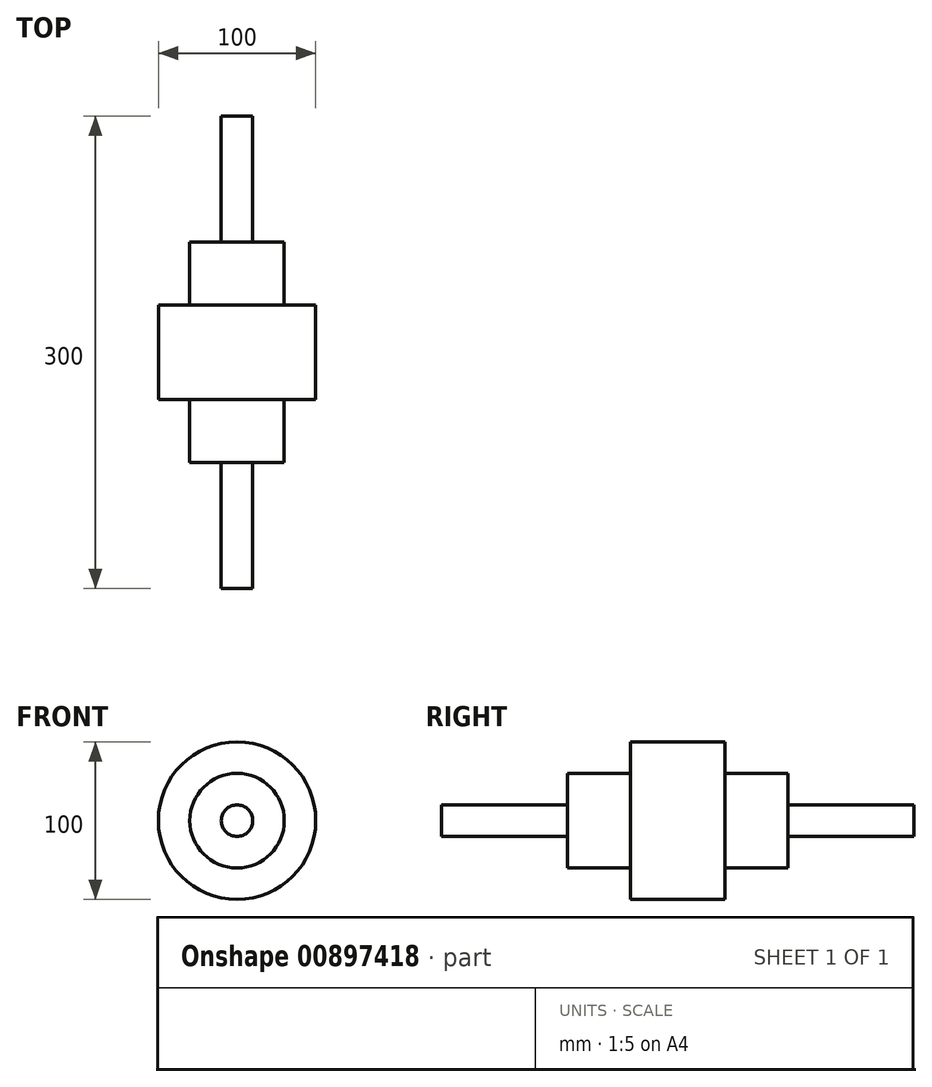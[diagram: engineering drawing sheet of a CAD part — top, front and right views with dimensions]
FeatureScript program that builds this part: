
annotation { "Feature Type Name" : "Feature", "Feature Type Description" : "" }
export const myFeature = defineFeature(function(context is Context, id is Id, definition is map)
    precondition{}
    {
        {
            var Q0;
            Q0=qCreatedBy(makeId("Front.planeOp"),FACE);
            var sketch = newSketch(context, id + "F0", { "sketchPlane" : qUnion([Q0])});
            skCircle(sketch, "E0", {"center": v(0, 0) * mm, "radius": 50 * mm});
            skSolve(sketch);
        }
        {
            var Q0;
            Q0=makeQuery(id+"F0.imprint","IMPRINT",FACE,{"disambiguationData":[TD([[makeQuery(id+"F0.imprint","IMPRINT",EDGE,{"derivedFrom":sQuery(id+"F0.wireOp",EDGE,"E0")}),1.0]])]});
            extrude(context, id + "F1", {"entities" : qUnion([Q0]), "depth" : 60 * mm, "offsetDistance" : 25.4 * mm});
        }
        {
            var Q0;
            Q0=makeQuery(id+"F1.opExtrude","CAP_FACE",FACE,{"disambiguationData":[OSD([sQuery(id+"F0.wireOp",EDGE,"E0")])],"isStart":false});
            var sketch = newSketch(context, id + "F2", { "sketchPlane" : qUnion([Q0])});
            skCircle(sketch, "E1", {"center": v(0, 0) * mm, "radius": 30 * mm});
            skSolve(sketch);
        }
        {
            var Q0;
            Q0=makeQuery(id+"F2.imprint","IMPRINT",FACE,{"disambiguationData":[TD([[makeQuery(id+"F2.imprint","IMPRINT",EDGE,{"derivedFrom":sQuery(id+"F2.wireOp",EDGE,"E1")}),1.0]])]});
            extrude(context, id + "F3", {"entities" : qUnion([Q0]), "operationType" : NewBodyOperationType.ADD, "depth" : 40 * mm, "offsetDistance" : 25.4 * mm});
        }
        {
            var Q0;
            Q0=makeQuery(id+"F3.opExtrude","CAP_FACE",FACE,{"disambiguationData":[OSD([sQuery(id+"F2.wireOp",EDGE,"E1")])],"isStart":false});
            var sketch = newSketch(context, id + "F4", { "sketchPlane" : qUnion([Q0])});
            skCircle(sketch, "E2", {"center": v(0, 0) * mm, "radius": 10 * mm});
            skSolve(sketch);
        }
        {
            var Q0;
            Q0=makeQuery(id+"F4.imprint","IMPRINT",FACE,{"disambiguationData":[TD([[makeQuery(id+"F4.imprint","IMPRINT",EDGE,{"derivedFrom":sQuery(id+"F4.wireOp",EDGE,"E2")}),1.0]])]});
            extrude(context, id + "F5", {"entities" : qUnion([Q0]), "operationType" : NewBodyOperationType.ADD, "depth" : 80 * mm, "offsetDistance" : 25.4 * mm});
        }
        {
            var Q0;
            Q0=makeQuery(id+"F1.opExtrude","CAP_FACE",FACE,{"disambiguationData":[OSD([sQuery(id+"F0.wireOp",EDGE,"E0")])],"isStart":true});
            var sketch = newSketch(context, id + "F6", { "sketchPlane" : qUnion([Q0])});
            skCircle(sketch, "E3", {"center": v(0, 0) * mm, "radius": 30 * mm});
            skSolve(sketch);
        }
        {
            var Q0;
            Q0=makeQuery(id+"F6.imprint","IMPRINT",FACE,{"disambiguationData":[TD([[makeQuery(id+"F6.imprint","IMPRINT",EDGE,{"derivedFrom":sQuery(id+"F6.wireOp",EDGE,"E3")}),1.0]])]});
            extrude(context, id + "F7", {"entities" : qUnion([Q0]), "operationType" : NewBodyOperationType.ADD, "depth" : 40 * mm, "offsetDistance" : 25.4 * mm});
        }
        {
            var Q0;
            Q0=makeQuery(id+"F7.opExtrude","CAP_FACE",FACE,{"disambiguationData":[OSD([sQuery(id+"F6.wireOp",EDGE,"E3")])],"isStart":false});
            var sketch = newSketch(context, id + "F8", { "sketchPlane" : qUnion([Q0])});
            skCircle(sketch, "E4", {"center": v(0, 0) * mm, "radius": 10 * mm});
            skSolve(sketch);
        }
        {
            var Q0;
            Q0 = qSketchRegion(id + "F8", true);
            extrude(context, id + "F9", {"entities" : qUnion([Q0]), "operationType" : NewBodyOperationType.ADD, "depth" : 80 * mm, "offsetDistance" : 25.4 * mm});
        }
    });
